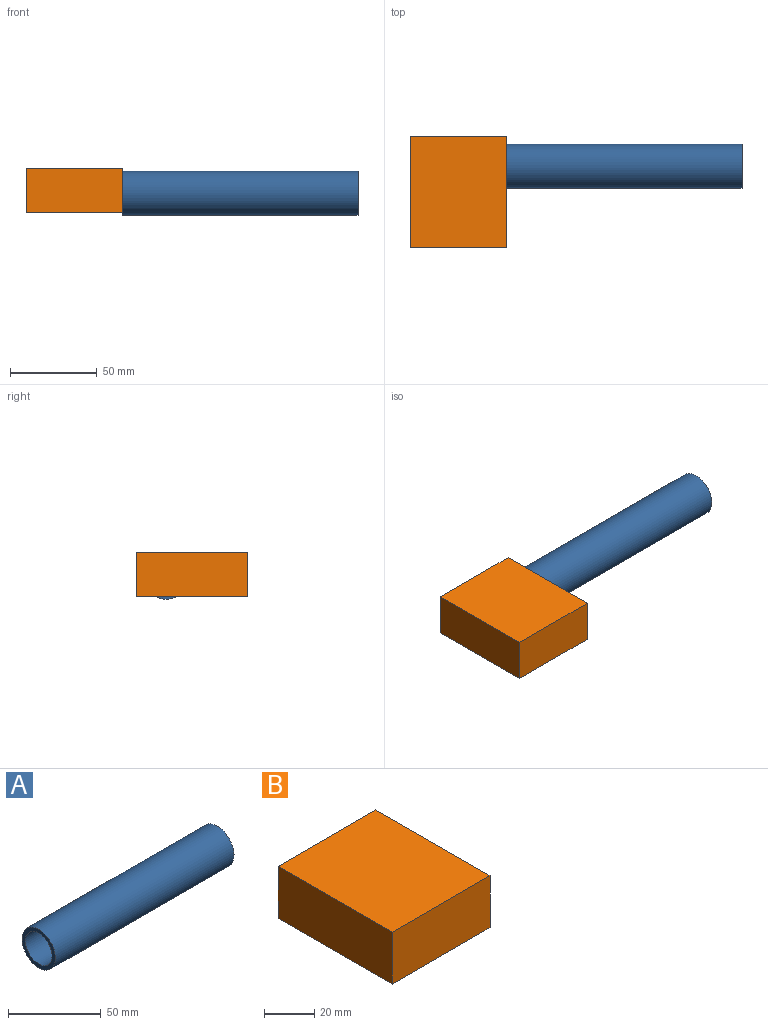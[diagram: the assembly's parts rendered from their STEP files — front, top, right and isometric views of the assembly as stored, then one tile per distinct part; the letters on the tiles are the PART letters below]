
ASSEMBLY  parts=2 mates=1
PART A: 4 faces, bbox 135.9x25.4x25.4 mm
  f0: cylinder r=12.7mm len=135.89mm, axis (-1,0,0), area 10843.5mm2, adj f1,f2
  f1: plane 25.4x25.4mm, normal (1,0,0), area 182.4mm2, adj f0,f3
  f2: plane 25.4x25.4mm, normal (-1,0,0), area 182.4mm2, adj f0,f3
  f3: cylinder r=10.16mm len=135.89mm, axis (-1,0,0), area 8674.8mm2, adj f1,f2
PART B: 6 faces, bbox 55.4x64.4x25.4 mm
  f0: plane 55.35x25.4mm, normal (0,1,0), area 1406mm2, adj f1,f3,f4,f5
  f1: plane 64.44x25.4mm, normal (-1,0,0), area 1636.9mm2, adj f0,f2,f4,f5
  f2: plane 55.35x25.4mm, normal (0,-1,0), area 1406mm2, adj f1,f3,f4,f5
  f3: plane 64.44x25.4mm, normal (1,0,0), area 1636.9mm2, adj f0,f2,f4,f5
  f4: plane 64.44x55.35mm, normal (0,0,1), area 3567.2mm2, adj f0,f1,f2,f3
  f5: plane 64.44x55.35mm, normal (0,0,-1), area 3567.2mm2, adj f0,f1,f2,f3
PLACE A t=(55.35,8.03,11.32)mm
PLACE B at identity fixed
MATE planar B.f3 <-> A.f0  axis (1,0,0) through (55.35,-6.82,12.7)mm
